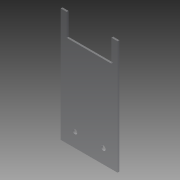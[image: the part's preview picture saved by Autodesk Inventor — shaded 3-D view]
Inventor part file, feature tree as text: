
AUTODESK INVENTOR PART (.ipt)
format: ipt  version: 2014 (Build 180170000, 170)  size: 86,016 bytes
history: native  units: in
note: dims shown in document units (in); Inventor stores cm internally (conversion verified against a paired STEP export)
features: extrude x1, sketch x1
ambient origin geometry x8: Origin, YZ Plane, XZ Plane, XY Plane, X Axis, Y Axis, Z Axis, Center Point
bodies: Solid1 (feature_tree)
feature tree (2):
  extrude  "Extrusion1"  Depth=4.0in
  sketch  "Sketch1"  dims[d0=2.0in d1=4.0in d2=4.0in d3=0.215in d4=0.79in d5=0.215in d6=0.163in d7=0.163in d8=0.5in d9=0.5in d10=0.5in d11=0.5in d12=0.0625in d13=0.0in]
